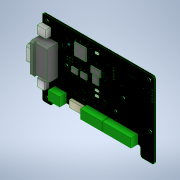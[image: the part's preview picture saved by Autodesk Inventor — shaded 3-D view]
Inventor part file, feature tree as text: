
AUTODESK INVENTOR PART (.ipt)
format: ipt  version: 2020 (Build 240168000, 168)  size: 1,196,544 bytes
history: native  units: in
note: dims shown in document units (in); Inventor stores cm internally (conversion verified against a paired STEP export)
features: extrude x21, other x19, sketch x4, fillet x1
ambient origin geometry x8: Origin, YZ Plane, XZ Plane, XY Plane, X Axis, Y Axis, Z Axis, Center Point
bodies: Solid1 (feature_tree)
feature tree (45):
  other  "Steering.brd"
  extrude  "Steering.brd_Outline"  Depth=0.063in
  extrude  "D2_2"  Depth=0.0394in TaperAngle=0.0deg
  extrude  "D3_4"  Depth=0.0394in TaperAngle=0.0deg
  extrude  "D4_6"  Depth=0.0984in TaperAngle=0.0deg
  extrude  "D7_8"  Depth=0.4921in TaperAngle=0.0deg
  extrude  "J1_10"  Depth=0.2756in TaperAngle=0.0deg
  extrude  "J3_12"  Depth=0.2756in TaperAngle=0.0deg
  extrude  "J4_14"  Depth=0.2756in TaperAngle=0.0deg
  extrude  "J5_16"  Depth=0.1969in TaperAngle=0.0deg
  extrude  "J6_18"  Depth=0.0394in TaperAngle=0.0deg
  extrude  "J7_20"  Depth=0.0394in TaperAngle=0.0deg
  extrude  "J8_22"  Depth=0.0394in TaperAngle=0.0deg
  extrude  "MC1_24"  Depth=0.0394in TaperAngle=0.0deg
  extrude  "S1_26"  Depth=0.0394in TaperAngle=0.0deg
  extrude  "U_3_28"  Depth=0.5118in
  extrude  "U1_30"  Depth=0.0787in TaperAngle=0.0deg
  extrude  "U2_32"  Depth=0.315in
  extrude  "Extrusion18"  Depth=0.6496in
  extrude  "Extrusion19"  Depth=0.1969in
  fillet  "Fillet1"  Radius=0.2461in
  extrude  "Hole Fixing"  Depth=0.0787in
  extrude  "Extrusion21"  Depth=0.2362in TaperAngle=0.0deg
  sketch  "Sketch1"  dims[d0=0.063in d1=0.0in d2=0.063in]
  other  "KINGBRIGHT_LED, LED_AA3528VRVCS_A_1"
  other  "KINGBRIGHT_LED, LED_AA3528VRVCS_A_3"
  other  "KINGBRIGHT_LED, PINK_5"
  other  "CHIP-LED0603, BLUE_7"
  other  "UX60-MB-5S8, UX60-MB-5S8_9"
  other  "MOLEX_5025850670, MOLEX_5025850670_11"
  other  "NONASSMANN_VGA_CONNECTOR, NONASSMANN_VGA_CONNECTOR_13"
  other  "SCREW_TERMINAL_PCB_CONN_8_POLE, PCB_SCREW_TERM_8_15"
  other  "SCREW_TERMINAL_PCB_CONN_6_POLE, PCB_SCREW_TERM_6_17"
  other  "SCREW_TERMINAL_PCB_CONN_3_POLE, PCB_SCREW_TERM_3_19"
  other  "B2PS-CENTERED, B2PS-VH_LF__SN__21"
  other  "TQFP44, ATMEGA32U4-AU_23"
  other  "CTS_DIP_SWITCH, CTS_SWITCH_SPST_25"
  other  "PTS645, PTS645_27"
  other  "TSSOP14, CD4066BPWR_29"
  other  "TSSOP14, CD4066BPWR_31"
  other  "Image1"
  sketch  "Sketch18"  dims[d3=0.0394in d4=0.0in d5=0.0394in d6=0.0in]
  sketch  "Sketch19"  dims[d7=0.0394in d8=0.0in d9=0.0394in d10=0.0in]
  other  "Patchwork_Repair"
  sketch  "Sketch21"  dims[d11=0.1969in d12=0.0in d13=0.0984in d14=0.0in d15=0.4921in d16=0.0in d17=0.2756in d18=0.0in d19=0.2756in d20=0.0in d21=0.2756in d22=0.0in d23=0.1969in d24=0.0in d25=0.0394in d26=0.0in d27=0.0394in d28=0.0in d29=0.0394in d30=0.0in d31=0.0394in d32=0.0in d33=0.0394in d34=0.0in d42=0.5118in d43=0.0787in d44=0.0in d45=0.315in d46=0.6496in d47=0.6135in d48=0.2461in d49=0.0787in d50=0.2362in d51=0.0in d52=0.0787in d54=1.7323in d55=0.3543in d56=0.0181in d57=2.246in d58=0.1969in d59=0.0in d60=0.1299in d61=0.1299in d62=1.1024in d63=1.1024in d64=1.4173in d65=2.9921in d66=0.0in d67=0.0in d68=0.3937in d69=0.7677in d70=0.1299in d71=0.2756in d72=0.1969in]
